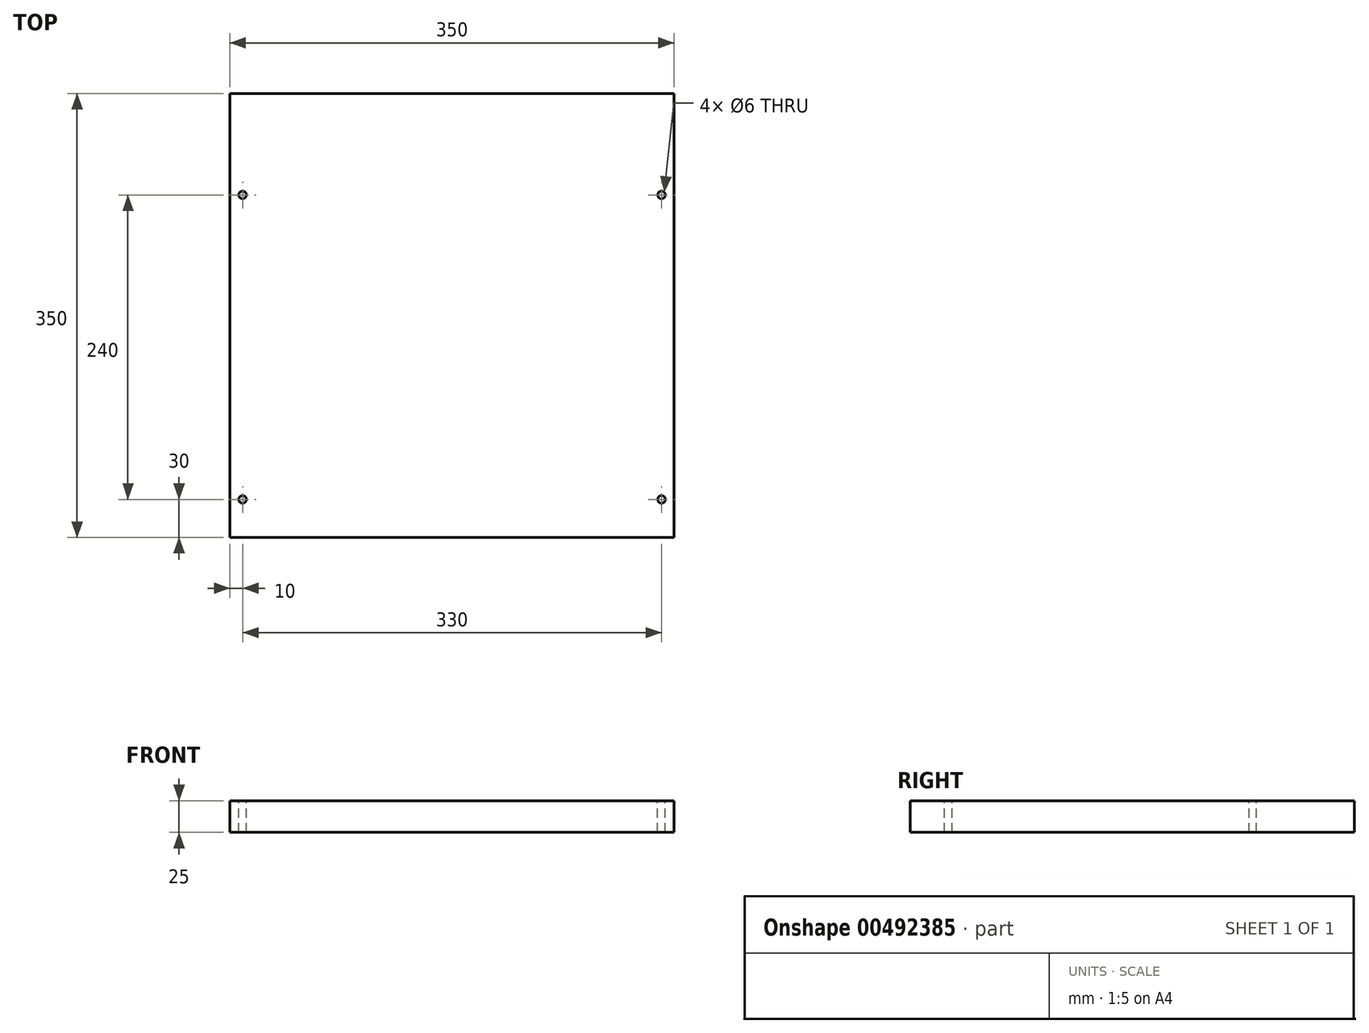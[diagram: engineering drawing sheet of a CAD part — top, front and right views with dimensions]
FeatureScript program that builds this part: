
annotation { "Feature Type Name" : "Feature", "Feature Type Description" : "" }
export const myFeature = defineFeature(function(context is Context, id is Id, definition is map)
    precondition{}
    {
        {
            var Q0;
            Q0=qCreatedBy(makeId("Top.planeOp"),FACE);
            var sketch = newSketch(context, id + "F0", { "sketchPlane" : qUnion([Q0])});
            skLineSegment(sketch, "E0.bottom", {"start": v(0, 0) * mm, "end": v(350, 0) * mm});
            skLineSegment(sketch, "E0.top", {"start": v(0, 300) * mm, "end": v(350, 300) * mm});
            skLineSegment(sketch, "E0.left", {"start": v(0, 0) * mm, "end": v(0, 300) * mm});
            skLineSegment(sketch, "E0.right", {"start": v(350, 0) * mm, "end": v(350, 300) * mm});
            skLineSegment(sketch, "E1.top", {"start": v(0, 350) * mm, "end": v(350, 350) * mm});
            skLineSegment(sketch, "E1.left", {"start": v(0, 300) * mm, "end": v(0, 350) * mm});
            skLineSegment(sketch, "E1.right", {"start": v(350, 300) * mm, "end": v(350, 350) * mm});
            skSolve(sketch);
        }
        {
            var Q0;
            Q0=qSketchRegion(id+"F0",true);
            extrude(context, id + "F1", {"entities" : qUnion([Q0]), "depth" : 25 * mm});
        }
        {
            var Q0;
            Q0=makeQuery(id+"F1.opExtrude","CAP_FACE",FACE,{"disambiguationData":[OSD([sQuery(id+"F0.wireOp",EDGE,"E0.bottom"),sQuery(id+"F0.wireOp",EDGE,"E0.left"),sQuery(id+"F0.wireOp",EDGE,"E0.right"),sQuery(id+"F0.wireOp",EDGE,"E1.top"),sQuery(id+"F0.wireOp",EDGE,"E1.left"),sQuery(id+"F0.wireOp",EDGE,"E1.right")])],"isStart":false});
            var sketch = newSketch(context, id + "F2", { "sketchPlane" : qUnion([Q0])});
            skCircle(sketch, "E2", {"center": v(10, 270) * mm, "radius": 3 * mm});
            skCircle(sketch, "E3", {"center": v(340, 270) * mm, "radius": 3 * mm});
            skCircle(sketch, "E4", {"center": v(340, 30) * mm, "radius": 3 * mm});
            skCircle(sketch, "E5", {"center": v(10, 30) * mm, "radius": 3 * mm});
            skSolve(sketch);
        }
        {
            var Q0;
            Q0=qSketchRegion(id+"F2",true);
            extrude(context, id + "F3", {"entities" : qUnion([Q0]), "operationType" : NewBodyOperationType.REMOVE, "endBound" : BoundingType.THROUGH_ALL, "oppositeDirection" : true, "depth" : 25 * mm});
        }
    });
